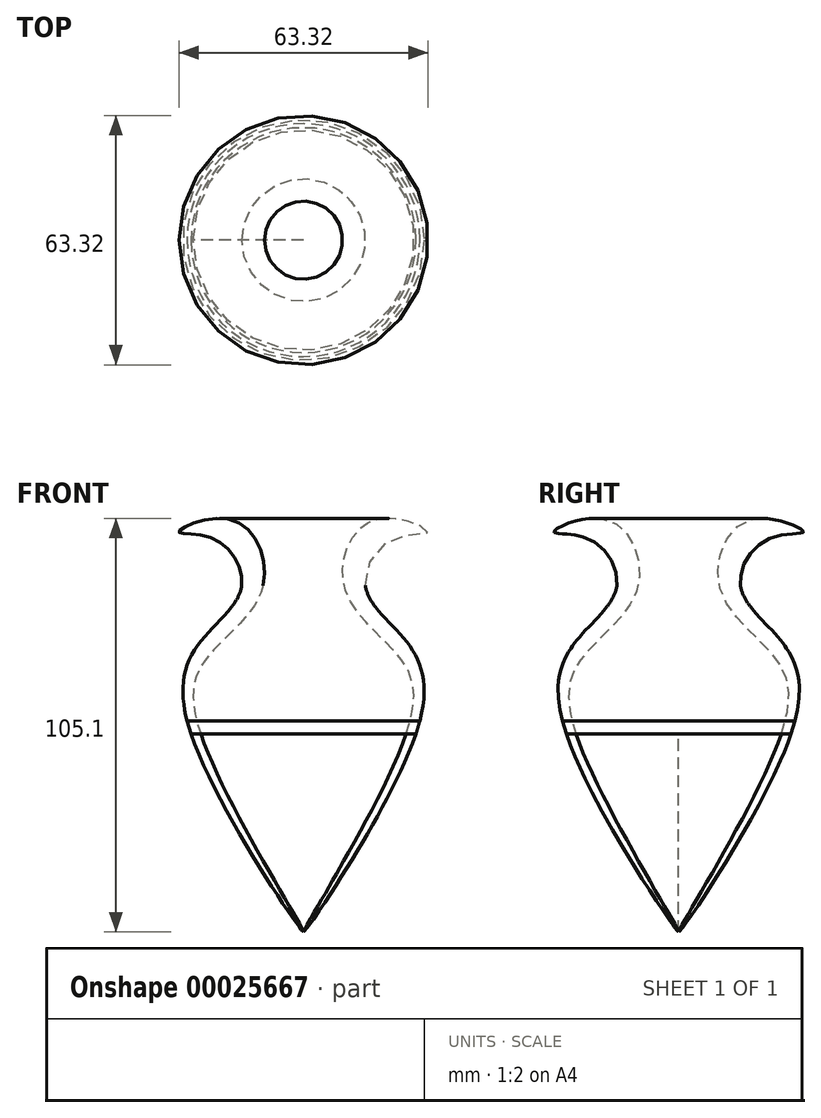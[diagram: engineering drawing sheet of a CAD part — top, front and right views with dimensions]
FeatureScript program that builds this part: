
annotation { "Feature Type Name" : "Feature", "Feature Type Description" : "" }
export const myFeature = defineFeature(function(context is Context, id is Id, definition is map)
    precondition{}
    {
        {
            var Q0;
            Q0=qCreatedBy(makeId("Front.planeOp"),FACE);
            var sketch = newSketch(context, id + "F0", { "sketchPlane" : qUnion([Q0])});
            skFitSpline(sketch, "E0", {"points": [v(0, -50.25) * mm, v(-28.56, 0) * mm, v(-25.56, 24.26) * mm, v(-15.7, 37.84) * mm, v(-23.4, 49.85) * mm, v(-31.66, 51.44) * mm, v(-18.42, 54.5) * mm, v(-10.26, 37.89) * mm, v(-23.56, 20.57) * mm, v(-26.09, 0) * mm, v(0, -50.25) * mm]});
            skLineSegment(sketch, "E1", {"start": v(0, 94.57) * mm, "end": v(0, -126.94) * mm});
            skArc(sketch, "E2", {"start": v(-15.7, 37.84) * mm, "mid": v(-23.27, 37.99) * mm, "end": v(-18.3, 32.26) * mm});
            skFitSpline(sketch, "E3.trimOffspring", {"points": [v(0, -50.25) * mm, v(-28.56, 0) * mm, v(-25.56, 24.26) * mm, v(-15.7, 37.84) * mm, v(-23.4, 49.85) * mm, v(-31.66, 51.44) * mm, v(-18.42, 54.5) * mm, v(-10.26, 37.89) * mm, v(-23.56, 20.57) * mm, v(-26.09, 0) * mm, v(0, -50.25) * mm]});
            skLineSegment(sketch, "E4", {"start": v(-29.57, 3.39) * mm, "end": v(-28.56, 0) * mm});
            skPoint(sketch, "E5.start.orphan", {"position": v(-30, 0) * mm});
            skLineSegment(sketch, "E6", {"start": v(-29.57, 3.39) * mm, "end": v(-28.56, 0) * mm});
            skLineSegment(sketch, "E7", {"start": v(-29.06, 1.7) * mm, "end": v(-28.56, 0) * mm});
            skLineSegment(sketch, "E8", {"start": v(-29.57, 3.39) * mm, "end": v(-29.06, 1.7) * mm});
            skSolve(sketch);
        }
        {
            var Q0;
            {var subQ0=sQuery(id+"F0.wireOp",EDGE,"E1");var subQ1=sQuery(id+"F0.wireOp",EDGE,"E0");var subQ3=makeQuery(id+"F0.imprint","INTERSECT",VERTEX,{"disambiguationData":[OD(0.0)],"derivedFrom":[subQ1,subQ0]});Q0=makeQuery(id+"F0.imprint","IMPRINT",FACE,{"disambiguationData":[TD([[makeQuery(id+"F0.imprint","IMPRINT",EDGE,{"disambiguationData":[TD([[subQ3,-1.0]])],"derivedFrom":subQ1}),-1.0]])]});}
            var Q1;
            Q1=sQuery(id+"F0.wireOp",EDGE,"E1");
            revolve(context, id + "F1", {"entities" : qUnion([Q0]), "axis" : qUnion([Q1]), "revolveType" : RevolveType.FULL});
        }
    });
